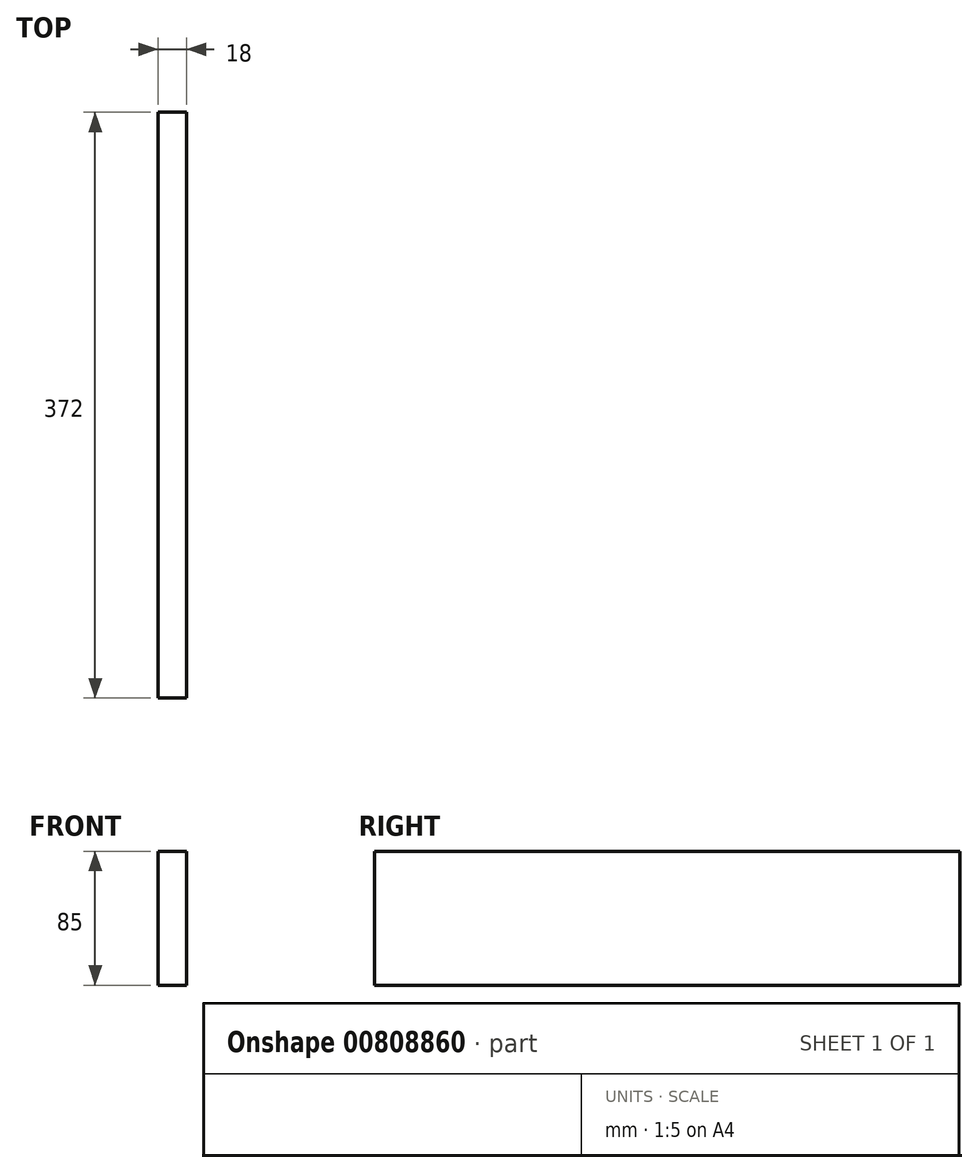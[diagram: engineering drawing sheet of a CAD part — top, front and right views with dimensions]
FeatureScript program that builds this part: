
annotation { "Feature Type Name" : "Feature", "Feature Type Description" : "" }
export const myFeature = defineFeature(function(context is Context, id is Id, definition is map)
    precondition{}
    {
        {
            var Q0;
            Q0=qCreatedBy(makeId("Right.planeOp"),FACE);
            var sketch = newSketch(context, id + "F0", { "sketchPlane" : qUnion([Q0])});
            skLineSegment(sketch, "E0.bottom", {"start": v(0, 0) * mm, "end": v(372, 0) * mm});
            skLineSegment(sketch, "E0.top", {"start": v(0, 85) * mm, "end": v(372, 85) * mm});
            skLineSegment(sketch, "E0.left", {"start": v(0, 0) * mm, "end": v(0, 85) * mm});
            skLineSegment(sketch, "E0.right", {"start": v(372, 0) * mm, "end": v(372, 85) * mm});
            skSolve(sketch);
        }
        {
            var Q0;
            Q0=makeQuery(id+"F0.imprint","IMPRINT",FACE,{"disambiguationData":[TD([[makeQuery(id+"F0.imprint","IMPRINT",EDGE,{"derivedFrom":sQuery(id+"F0.wireOp",EDGE,"E0.bottom")}),1.0]])]});
            var Q1;
            Q1=sQuery(id+"F0.wireOp",EDGE,"E0.top");
            var Q2;
            Q2=sQuery(id+"F0.wireOp",EDGE,"E0.left");
            var Q3;
            Q3=sQuery(id+"F0.wireOp",EDGE,"E0.right");
            var Q4;
            Q4=sQuery(id+"F0.wireOp",EDGE,"E0.bottom");
            extrude(context, id + "F1", {"entities" : qUnion([Q0]), "surfaceEntities" : qUnion([Q1, Q2, Q3, Q4]), "depth" : 18 * mm, "offsetDistance" : 25 * mm});
        }
    });
